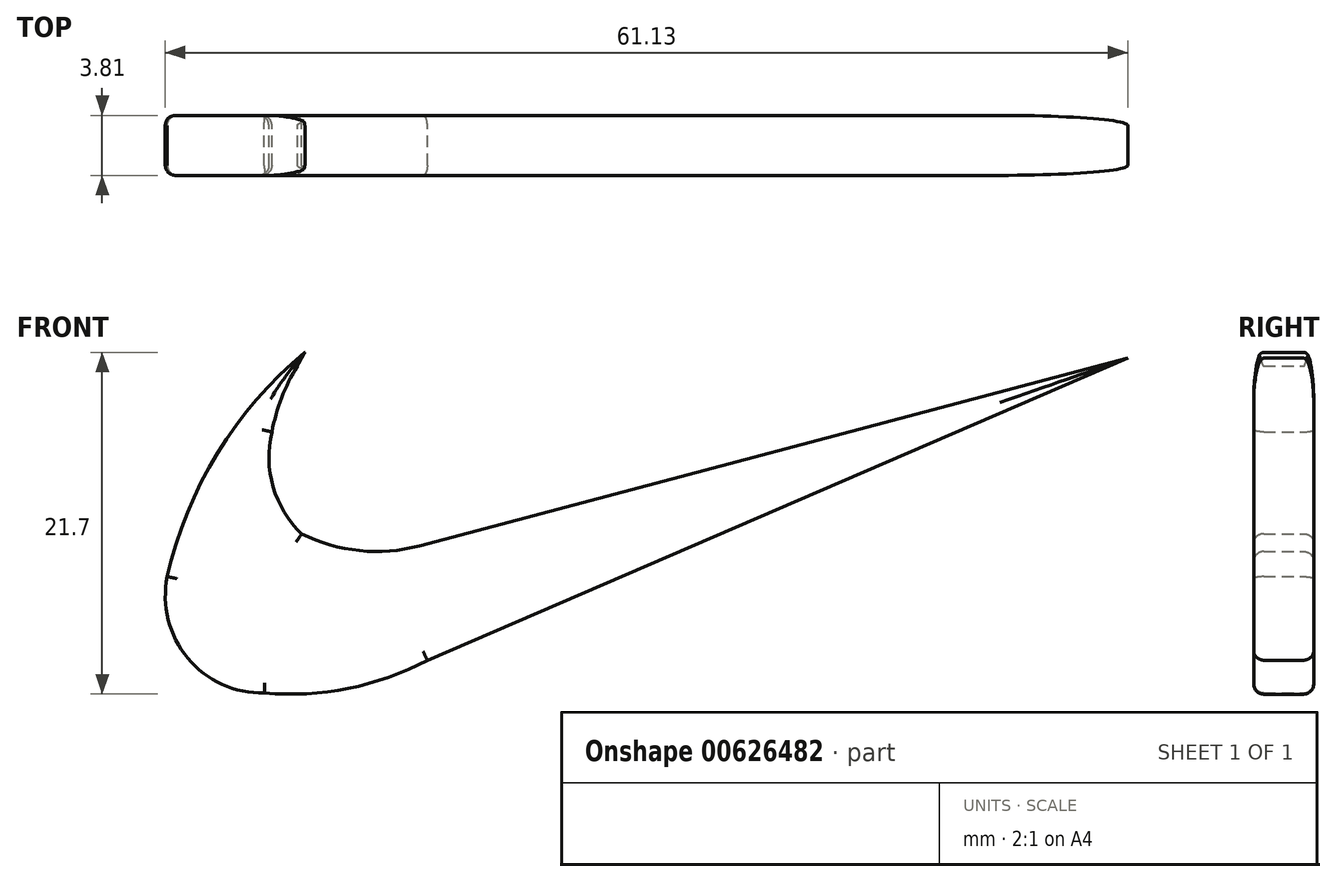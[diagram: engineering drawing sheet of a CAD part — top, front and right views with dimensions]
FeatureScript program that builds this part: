
annotation { "Feature Type Name" : "Feature", "Feature Type Description" : "" }
export const myFeature = defineFeature(function(context is Context, id is Id, definition is map)
    precondition{}
    {
        {
            var Q0;
            Q0=qCreatedBy(makeId("Front.planeOp"),FACE);
            var sketch = newSketch(context, id + "F0", { "sketchPlane" : qUnion([Q0])});
            skArc(sketch, "E0", {"start": v(-59.54, 48.5) * mm, "mid": v(-65.09, 42.1) * mm, "end": v(-68.27, 34.26) * mm});
            skArc(sketch, "E1", {"start": v(-68.27, 34.26) * mm, "mid": v(-66.97, 29.08) * mm, "end": v(-62.1, 26.87) * mm});
            skArc(sketch, "E2", {"start": v(-62.1, 26.87) * mm, "mid": v(-56.78, 27.16) * mm, "end": v(-51.75, 28.95) * mm});
            skLineSegment(sketch, "E3", {"start": v(-51.75, 28.95) * mm, "end": v(-7.27, 48.13) * mm});
            skLineSegment(sketch, "E4", {"start": v(-7.27, 48.13) * mm, "end": v(-52.25, 36.21) * mm});
            skArc(sketch, "E5", {"start": v(-59.73, 36.99) * mm, "mid": v(-56.06, 35.92) * mm, "end": v(-52.25, 36.21) * mm});
            skArc(sketch, "E6", {"start": v(-61.63, 43.46) * mm, "mid": v(-61.55, 39.97) * mm, "end": v(-59.73, 36.99) * mm});
            skArc(sketch, "E7", {"start": v(-60.01, 47.64) * mm, "mid": v(-61, 45.62) * mm, "end": v(-61.63, 43.46) * mm});
            skLineSegment(sketch, "E8", {"start": v(-60.01, 47.64) * mm, "end": v(-59.54, 48.5) * mm});
            skSolve(sketch);
        }
        {
            var Q0;
            Q0=makeQuery(id+"F0.imprint","IMPRINT",FACE,{"disambiguationData":[TD([[makeQuery(id+"F0.imprint","IMPRINT",EDGE,{"derivedFrom":sQuery(id+"F0.wireOp",EDGE,"E0")}),1.0]])]});
            extrude(context, id + "F1", {"entities" : qUnion([Q0]), "depth" : 3.8 * mm, "offsetDistance" : 25.4 * mm});
        }
        {
            var Q0;
            Q0=makeQuery(id+"F1.opExtrude","CAP_EDGE",EDGE,{"disambiguationData":[OSD([sQuery(id+"F0.wireOp",EDGE,"E7")])],"isStart":false});
            var Q1;
            Q1=makeQuery(id+"F1.opExtrude","CAP_EDGE",EDGE,{"disambiguationData":[OSD([sQuery(id+"F0.wireOp",EDGE,"E8")])],"isStart":false});
            var Q2;
            Q2=makeQuery(id+"F1.opExtrude","CAP_EDGE",EDGE,{"disambiguationData":[OSD([sQuery(id+"F0.wireOp",EDGE,"E6")])],"isStart":false});
            var Q3;
            Q3=makeQuery(id+"F1.opExtrude","CAP_EDGE",EDGE,{"disambiguationData":[OSD([sQuery(id+"F0.wireOp",EDGE,"E5")])],"isStart":false});
            var Q4;
            Q4=makeQuery(id+"F1.opExtrude","CAP_EDGE",EDGE,{"disambiguationData":[OSD([sQuery(id+"F0.wireOp",EDGE,"E4")])],"isStart":false});
            var Q5;
            Q5=makeQuery(id+"F1.opExtrude","CAP_EDGE",EDGE,{"disambiguationData":[OSD([sQuery(id+"F0.wireOp",EDGE,"E3")])],"isStart":false});
            var Q6;
            Q6=makeQuery(id+"F1.opExtrude","CAP_EDGE",EDGE,{"disambiguationData":[OSD([sQuery(id+"F0.wireOp",EDGE,"E2")])],"isStart":false});
            var Q7;
            Q7=makeQuery(id+"F1.opExtrude","CAP_EDGE",EDGE,{"disambiguationData":[OSD([sQuery(id+"F0.wireOp",EDGE,"E1")])],"isStart":false});
            var Q8;
            Q8=makeQuery(id+"F1.opExtrude","CAP_EDGE",EDGE,{"disambiguationData":[OSD([sQuery(id+"F0.wireOp",EDGE,"E0")])],"isStart":false});
            fillet(context, id + "F2", {"entities" : qUnion([Q0, Q1, Q2, Q3, Q4, Q5, Q6, Q7, Q8]), "radius" : 0.64 * mm, "tangentPropagation" : true, "allowEdgeOverflow" : false});
        }
        {
            var Q0;
            Q0=makeQuery(id+"F1.opExtrude","CAP_EDGE",EDGE,{"disambiguationData":[OSD([sQuery(id+"F0.wireOp",EDGE,"E0")])],"isStart":true});
            var Q1;
            Q1=makeQuery(id+"F1.opExtrude","CAP_EDGE",EDGE,{"disambiguationData":[OSD([sQuery(id+"F0.wireOp",EDGE,"E1")])],"isStart":true});
            var Q2;
            Q2=makeQuery(id+"F1.opExtrude","CAP_EDGE",EDGE,{"disambiguationData":[OSD([sQuery(id+"F0.wireOp",EDGE,"E2")])],"isStart":true});
            var Q3;
            Q3=makeQuery(id+"F1.opExtrude","CAP_EDGE",EDGE,{"disambiguationData":[OSD([sQuery(id+"F0.wireOp",EDGE,"E3")])],"isStart":true});
            var Q4;
            Q4=makeQuery(id+"F1.opExtrude","CAP_EDGE",EDGE,{"disambiguationData":[OSD([sQuery(id+"F0.wireOp",EDGE,"E4")])],"isStart":true});
            var Q5;
            Q5=makeQuery(id+"F1.opExtrude","CAP_EDGE",EDGE,{"disambiguationData":[OSD([sQuery(id+"F0.wireOp",EDGE,"E5")])],"isStart":true});
            var Q6;
            Q6=makeQuery(id+"F1.opExtrude","CAP_EDGE",EDGE,{"disambiguationData":[OSD([sQuery(id+"F0.wireOp",EDGE,"E6")])],"isStart":true});
            var Q7;
            Q7=makeQuery(id+"F1.opExtrude","CAP_EDGE",EDGE,{"disambiguationData":[OSD([sQuery(id+"F0.wireOp",EDGE,"E7")])],"isStart":true});
            var Q8;
            Q8=makeQuery(id+"F1.opExtrude","CAP_EDGE",EDGE,{"disambiguationData":[OSD([sQuery(id+"F0.wireOp",EDGE,"E8")])],"isStart":true});
            fillet(context, id + "F3", {"entities" : qUnion([Q0, Q1, Q2, Q3, Q4, Q5, Q6, Q7, Q8]), "radius" : 0.64 * mm, "tangentPropagation" : true, "allowEdgeOverflow" : false});
        }
    });
